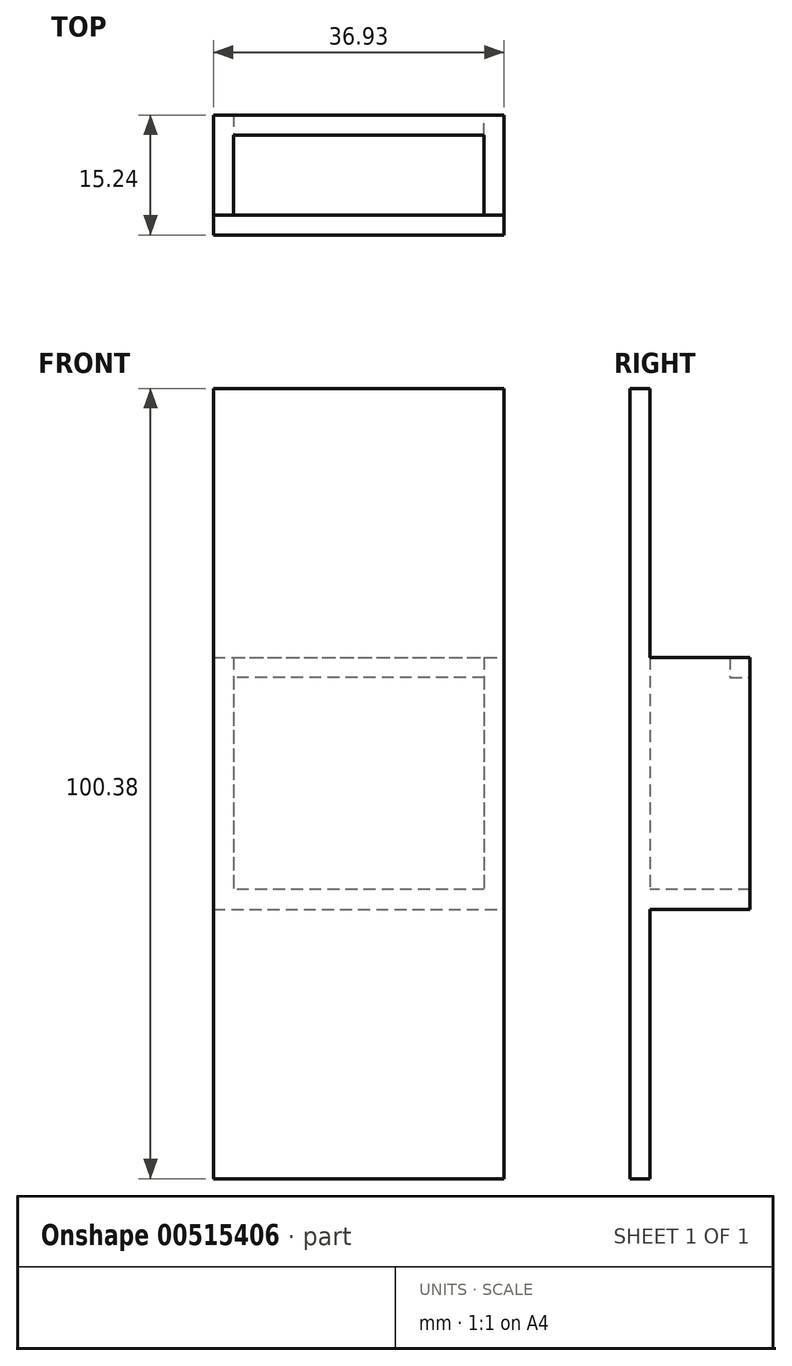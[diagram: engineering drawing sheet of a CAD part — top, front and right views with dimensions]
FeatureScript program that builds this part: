
annotation { "Feature Type Name" : "Feature", "Feature Type Description" : "" }
export const myFeature = defineFeature(function(context is Context, id is Id, definition is map)
    precondition{}
    {
        {
            var Q0;
            Q0=qCreatedBy(makeId("Front.planeOp"),FACE);
            var sketch = newSketch(context, id + "F0", { "sketchPlane" : qUnion([Q0])});
            skLineSegment(sketch, "E0.bottom", {"start": v(-22.03, 50.6) * mm, "end": v(14.9, 50.6) * mm});
            skLineSegment(sketch, "E0.top", {"start": v(-22.03, -49.78) * mm, "end": v(14.9, -49.78) * mm});
            skLineSegment(sketch, "E0.left", {"start": v(-22.03, 50.6) * mm, "end": v(-22.03, -49.78) * mm});
            skLineSegment(sketch, "E0.right", {"start": v(14.9, 50.6) * mm, "end": v(14.9, -49.78) * mm});
            skSolve(sketch);
        }
        {
            var Q0;
            Q0 = qSketchRegion(id + "F0", true);
            extrude(context, id + "F1", {"entities" : qUnion([Q0]), "depth" : 2.54 * mm, "offsetDistance" : 25.4 * mm});
        }
        {
            var Q0;
            Q0=makeQuery(id+"F1.opExtrude","CAP_FACE",FACE,{"disambiguationData":[OSD([sQuery(id+"F0.wireOp",EDGE,"E0.bottom"),sQuery(id+"F0.wireOp",EDGE,"E0.top"),sQuery(id+"F0.wireOp",EDGE,"E0.left"),sQuery(id+"F0.wireOp",EDGE,"E0.right")])],"isStart":false});
            var sketch = newSketch(context, id + "F2", { "sketchPlane" : qUnion([Q0])});
            skLineSegment(sketch, "E1.bottom", {"start": v(-22.03, 16.4) * mm, "end": v(14.9, 16.4) * mm});
            skLineSegment(sketch, "E1.top", {"start": v(-22.03, -15.6) * mm, "end": v(14.9, -15.6) * mm});
            skLineSegment(sketch, "E1.left", {"start": v(-22.03, 16.4) * mm, "end": v(-22.03, -15.6) * mm});
            skLineSegment(sketch, "E1.right", {"start": v(14.9, 16.4) * mm, "end": v(14.9, -15.6) * mm});
            skSolve(sketch);
        }
        {
            var Q0;
            Q0=makeQuery(id+"F2.imprint","IMPRINT",FACE,{"disambiguationData":[TD([[makeQuery(id+"F2.imprint","IMPRINT",EDGE,{"derivedFrom":sQuery(id+"F2.wireOp",EDGE,"E1.bottom")}),-1.0]])]});
            extrude(context, id + "F3", {"entities" : qUnion([Q0]), "operationType" : NewBodyOperationType.ADD, "oppositeDirection" : true, "depth" : 15.24 * mm, "offsetDistance" : 25.4 * mm});
        }
        {
            var Q0;
            Q0=makeQuery(id+"F3.opExtrude","SWEPT_FACE",FACE,{"disambiguationData":[OSD([sQuery(id+"F2.wireOp",EDGE,"E1.bottom")])]});
            shell(context, id + "F4", {"entities" : qUnion([Q0]), "thickness" : 2.54 * mm});
        }
        {
            var Q0;
            Q0=makeQuery(id+"F3.opExtrude","CAP_FACE",FACE,{"disambiguationData":[OSD([sQuery(id+"F2.wireOp",EDGE,"E1.bottom"),sQuery(id+"F2.wireOp",EDGE,"E1.top"),sQuery(id+"F2.wireOp",EDGE,"E1.left"),sQuery(id+"F2.wireOp",EDGE,"E1.right")])],"isStart":false});
            var sketch = newSketch(context, id + "F5", { "sketchPlane" : qUnion([Q0])});
            skLineSegment(sketch, "E2.bottom", {"start": v(-12.36, 13.86) * mm, "end": v(19.49, 13.86) * mm});
            skLineSegment(sketch, "E2.top", {"start": v(-12.36, -13.06) * mm, "end": v(19.49, -13.06) * mm});
            skLineSegment(sketch, "E2.left", {"start": v(-12.36, 13.86) * mm, "end": v(-12.36, -13.06) * mm});
            skLineSegment(sketch, "E2.right", {"start": v(19.49, 13.86) * mm, "end": v(19.49, -13.06) * mm});
            skSolve(sketch);
        }
        {
            var Q0;
            Q0 = qSketchRegion(id + "F5", true);
            extrude(context, id + "F6", {"entities" : qUnion([Q0]), "operationType" : NewBodyOperationType.REMOVE, "endBound" : BoundingType.UP_TO_NEXT, "oppositeDirection" : true, "depth" : 25.4 * mm, "offsetDistance" : 25.4 * mm});
        }
    });
